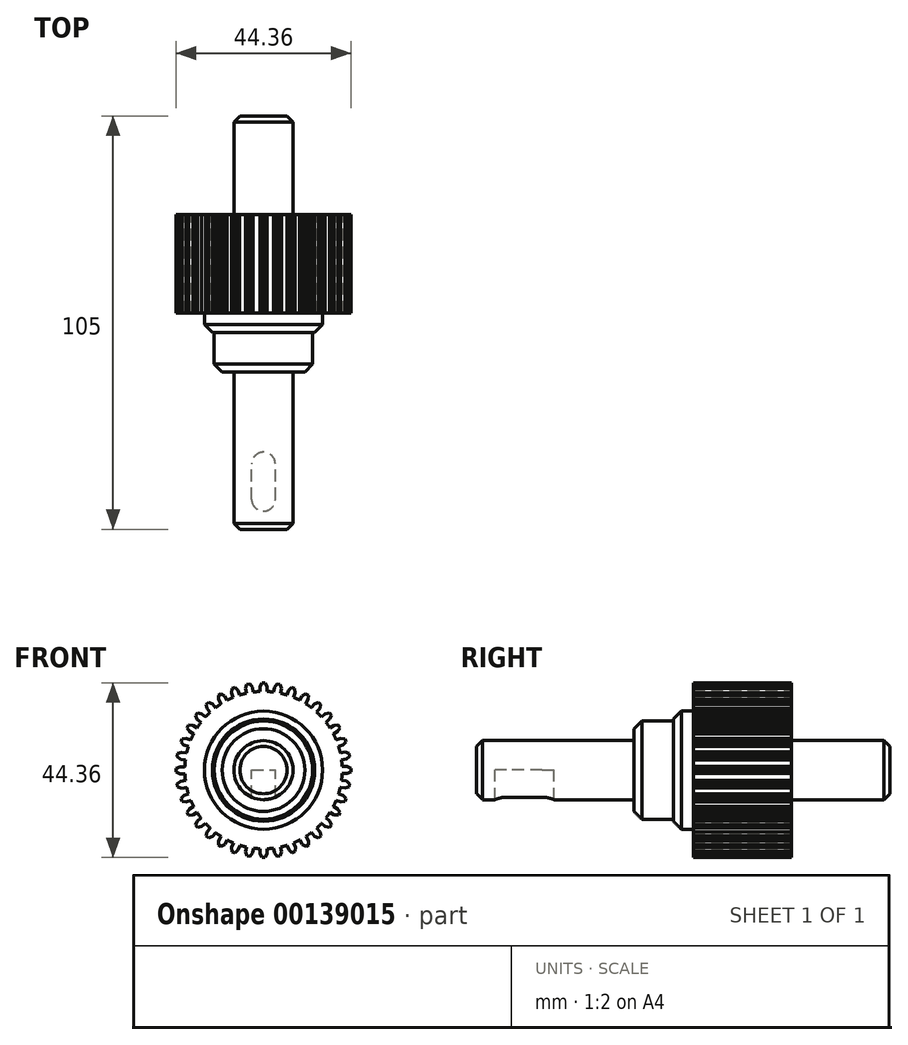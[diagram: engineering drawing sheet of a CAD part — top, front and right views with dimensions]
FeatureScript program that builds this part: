
annotation { "Feature Type Name" : "Feature", "Feature Type Description" : "" }
export const myFeature = defineFeature(function(context is Context, id is Id, definition is map)
    precondition{}
    {
        {
            var Q0;
            Q0=qCreatedBy(makeId("Front.planeOp"),FACE);
            var sketch = newSketch(context, id + "F0", { "sketchPlane" : qUnion([Q0])});
            skCircle(sketch, "E0", {"center": v(0, 0) * mm, "radius": 20 * mm});
            skLineSegment(sketch, "E1", {"start": v(-0.91, 19.98) * mm, "end": v(-0.91, 21.22) * mm});
            skLineSegment(sketch, "E2", {"start": v(-0.91, 21.22) * mm, "end": v(-0.42, 22.18) * mm});
            skLineSegment(sketch, "E3", {"start": v(-0.42, 22.18) * mm, "end": v(0.39, 22.18) * mm});
            skLineSegment(sketch, "E4", {"start": v(0.39, 22.18) * mm, "end": v(0.87, 21.22) * mm});
            skLineSegment(sketch, "E5", {"start": v(0.87, 21.22) * mm, "end": v(0.87, 19.98) * mm});
            skLineSegment(sketch, "E6", {"start": v(0, 0) * mm, "end": v(-0.02, 25.08) * mm});
            skPoint(sketch, "E6.endSnap0", {"position": v(-0.02, 22.18) * mm});
            skLineSegment(sketch, "E7.1.0", {"start": v(-4.37, 19.52) * mm, "end": v(-4.58, 20.74) * mm});
            skLineSegment(sketch, "E7.1.1", {"start": v(-4.58, 20.74) * mm, "end": v(-4.27, 21.77) * mm});
            skLineSegment(sketch, "E7.1.2", {"start": v(-4.27, 21.77) * mm, "end": v(-3.47, 21.91) * mm});
            skLineSegment(sketch, "E7.1.3", {"start": v(-3.47, 21.91) * mm, "end": v(-2.83, 21.05) * mm});
            skLineSegment(sketch, "E7.1.4", {"start": v(-2.83, 21.05) * mm, "end": v(-2.61, 19.83) * mm});
            skLineSegment(sketch, "E7.2.0", {"start": v(-7.69, 18.46) * mm, "end": v(-8.11, 19.63) * mm});
            skLineSegment(sketch, "E7.2.1", {"start": v(-8.11, 19.63) * mm, "end": v(-7.98, 20.7) * mm});
            skLineSegment(sketch, "E7.2.2", {"start": v(-7.98, 20.7) * mm, "end": v(-7.22, 20.98) * mm});
            skLineSegment(sketch, "E7.2.3", {"start": v(-7.22, 20.98) * mm, "end": v(-6.44, 20.24) * mm});
            skLineSegment(sketch, "E7.2.4", {"start": v(-6.44, 20.24) * mm, "end": v(-6.01, 19.07) * mm});
            skLineSegment(sketch, "E7.3.0", {"start": v(-10.78, 16.85) * mm, "end": v(-11.4, 17.92) * mm});
            skLineSegment(sketch, "E7.3.1", {"start": v(-11.4, 17.92) * mm, "end": v(-11.46, 19) * mm});
            skLineSegment(sketch, "E7.3.2", {"start": v(-11.46, 19) * mm, "end": v(-10.76, 19.4) * mm});
            skLineSegment(sketch, "E7.3.3", {"start": v(-10.76, 19.4) * mm, "end": v(-9.86, 18.81) * mm});
            skLineSegment(sketch, "E7.3.4", {"start": v(-9.86, 18.81) * mm, "end": v(-9.24, 17.74) * mm});
            skLineSegment(sketch, "E7.4.0", {"start": v(-13.54, 14.72) * mm, "end": v(-14.34, 15.67) * mm});
            skLineSegment(sketch, "E7.4.1", {"start": v(-14.34, 15.67) * mm, "end": v(-14.58, 16.72) * mm});
            skLineSegment(sketch, "E7.4.2", {"start": v(-14.58, 16.72) * mm, "end": v(-13.96, 17.24) * mm});
            skLineSegment(sketch, "E7.4.3", {"start": v(-13.96, 17.24) * mm, "end": v(-12.97, 16.82) * mm});
            skLineSegment(sketch, "E7.4.4", {"start": v(-12.97, 16.82) * mm, "end": v(-12.18, 15.87) * mm});
            skLineSegment(sketch, "E7.5.0", {"start": v(-15.9, 12.14) * mm, "end": v(-16.84, 12.94) * mm});
            skLineSegment(sketch, "E7.5.1", {"start": v(-16.84, 12.94) * mm, "end": v(-17.26, 13.93) * mm});
            skLineSegment(sketch, "E7.5.2", {"start": v(-17.26, 13.93) * mm, "end": v(-16.74, 14.55) * mm});
            skLineSegment(sketch, "E7.5.3", {"start": v(-16.74, 14.55) * mm, "end": v(-15.7, 14.3) * mm});
            skLineSegment(sketch, "E7.5.4", {"start": v(-15.7, 14.3) * mm, "end": v(-14.75, 13.51) * mm});
            skLineSegment(sketch, "E7.6.0", {"start": v(-17.76, 9.2) * mm, "end": v(-18.83, 9.82) * mm});
            skLineSegment(sketch, "E7.6.1", {"start": v(-18.83, 9.82) * mm, "end": v(-19.42, 10.72) * mm});
            skLineSegment(sketch, "E7.6.2", {"start": v(-19.42, 10.72) * mm, "end": v(-19.02, 11.43) * mm});
            skLineSegment(sketch, "E7.6.3", {"start": v(-19.02, 11.43) * mm, "end": v(-17.94, 11.37) * mm});
            skLineSegment(sketch, "E7.6.4", {"start": v(-17.94, 11.37) * mm, "end": v(-16.87, 10.75) * mm});
            skLineSegment(sketch, "E7.7.0", {"start": v(-19.09, 5.98) * mm, "end": v(-20.25, 6.4) * mm});
            skLineSegment(sketch, "E7.7.1", {"start": v(-20.25, 6.4) * mm, "end": v(-20.99, 7.19) * mm});
            skLineSegment(sketch, "E7.7.2", {"start": v(-20.99, 7.19) * mm, "end": v(-20.71, 7.95) * mm});
            skLineSegment(sketch, "E7.7.3", {"start": v(-20.71, 7.95) * mm, "end": v(-19.64, 8.08) * mm});
            skLineSegment(sketch, "E7.7.4", {"start": v(-19.64, 8.08) * mm, "end": v(-18.48, 7.65) * mm});
            skLineSegment(sketch, "E7.8.0", {"start": v(-19.83, 2.57) * mm, "end": v(-21.06, 2.79) * mm});
            skLineSegment(sketch, "E7.8.1", {"start": v(-21.06, 2.79) * mm, "end": v(-21.92, 3.44) * mm});
            skLineSegment(sketch, "E7.8.2", {"start": v(-21.92, 3.44) * mm, "end": v(-21.78, 4.23) * mm});
            skLineSegment(sketch, "E7.8.3", {"start": v(-21.78, 4.23) * mm, "end": v(-20.75, 4.54) * mm});
            skLineSegment(sketch, "E7.8.4", {"start": v(-20.75, 4.54) * mm, "end": v(-19.53, 4.33) * mm});
            skLineSegment(sketch, "E7.9.0", {"start": v(-19.98, -0.91) * mm, "end": v(-21.22, -0.91) * mm});
            skLineSegment(sketch, "E7.9.1", {"start": v(-21.22, -0.91) * mm, "end": v(-22.18, -0.42) * mm});
            skLineSegment(sketch, "E7.9.2", {"start": v(-22.18, -0.42) * mm, "end": v(-22.18, 0.39) * mm});
            skLineSegment(sketch, "E7.9.3", {"start": v(-22.18, 0.39) * mm, "end": v(-21.22, 0.87) * mm});
            skLineSegment(sketch, "E7.9.4", {"start": v(-21.22, 0.87) * mm, "end": v(-19.98, 0.87) * mm});
            skLineSegment(sketch, "E7.10.0", {"start": v(-19.52, -4.37) * mm, "end": v(-20.74, -4.58) * mm});
            skLineSegment(sketch, "E7.10.1", {"start": v(-20.74, -4.58) * mm, "end": v(-21.77, -4.27) * mm});
            skLineSegment(sketch, "E7.10.2", {"start": v(-21.77, -4.27) * mm, "end": v(-21.91, -3.47) * mm});
            skLineSegment(sketch, "E7.10.3", {"start": v(-21.91, -3.47) * mm, "end": v(-21.05, -2.83) * mm});
            skLineSegment(sketch, "E7.10.4", {"start": v(-21.05, -2.83) * mm, "end": v(-19.83, -2.61) * mm});
            skLineSegment(sketch, "E7.11.0", {"start": v(-18.46, -7.69) * mm, "end": v(-19.63, -8.11) * mm});
            skLineSegment(sketch, "E7.11.1", {"start": v(-19.63, -8.11) * mm, "end": v(-20.7, -7.98) * mm});
            skLineSegment(sketch, "E7.11.2", {"start": v(-20.7, -7.98) * mm, "end": v(-20.98, -7.22) * mm});
            skLineSegment(sketch, "E7.11.3", {"start": v(-20.98, -7.22) * mm, "end": v(-20.24, -6.44) * mm});
            skLineSegment(sketch, "E7.11.4", {"start": v(-20.24, -6.44) * mm, "end": v(-19.07, -6.01) * mm});
            skLineSegment(sketch, "E7.12.0", {"start": v(-16.85, -10.78) * mm, "end": v(-17.92, -11.4) * mm});
            skLineSegment(sketch, "E7.12.1", {"start": v(-17.92, -11.4) * mm, "end": v(-19, -11.46) * mm});
            skLineSegment(sketch, "E7.12.2", {"start": v(-19, -11.46) * mm, "end": v(-19.4, -10.76) * mm});
            skLineSegment(sketch, "E7.12.3", {"start": v(-19.4, -10.76) * mm, "end": v(-18.81, -9.86) * mm});
            skLineSegment(sketch, "E7.12.4", {"start": v(-18.81, -9.86) * mm, "end": v(-17.74, -9.24) * mm});
            skLineSegment(sketch, "E7.13.0", {"start": v(-14.72, -13.54) * mm, "end": v(-15.67, -14.34) * mm});
            skLineSegment(sketch, "E7.13.1", {"start": v(-15.67, -14.34) * mm, "end": v(-16.72, -14.58) * mm});
            skLineSegment(sketch, "E7.13.2", {"start": v(-16.72, -14.58) * mm, "end": v(-17.24, -13.96) * mm});
            skLineSegment(sketch, "E7.13.3", {"start": v(-17.24, -13.96) * mm, "end": v(-16.82, -12.97) * mm});
            skLineSegment(sketch, "E7.13.4", {"start": v(-16.82, -12.97) * mm, "end": v(-15.87, -12.18) * mm});
            skLineSegment(sketch, "E7.14.0", {"start": v(-12.14, -15.9) * mm, "end": v(-12.94, -16.84) * mm});
            skLineSegment(sketch, "E7.14.1", {"start": v(-12.94, -16.84) * mm, "end": v(-13.93, -17.26) * mm});
            skLineSegment(sketch, "E7.14.2", {"start": v(-13.93, -17.26) * mm, "end": v(-14.55, -16.74) * mm});
            skLineSegment(sketch, "E7.14.3", {"start": v(-14.55, -16.74) * mm, "end": v(-14.3, -15.7) * mm});
            skLineSegment(sketch, "E7.14.4", {"start": v(-14.3, -15.7) * mm, "end": v(-13.51, -14.75) * mm});
            skLineSegment(sketch, "E7.15.0", {"start": v(-9.2, -17.76) * mm, "end": v(-9.82, -18.83) * mm});
            skLineSegment(sketch, "E7.15.1", {"start": v(-9.82, -18.83) * mm, "end": v(-10.72, -19.42) * mm});
            skLineSegment(sketch, "E7.15.2", {"start": v(-10.72, -19.42) * mm, "end": v(-11.43, -19.02) * mm});
            skLineSegment(sketch, "E7.15.3", {"start": v(-11.43, -19.02) * mm, "end": v(-11.37, -17.94) * mm});
            skLineSegment(sketch, "E7.15.4", {"start": v(-11.37, -17.94) * mm, "end": v(-10.75, -16.87) * mm});
            skLineSegment(sketch, "E7.16.0", {"start": v(-5.98, -19.09) * mm, "end": v(-6.4, -20.25) * mm});
            skLineSegment(sketch, "E7.16.1", {"start": v(-6.4, -20.25) * mm, "end": v(-7.19, -20.99) * mm});
            skLineSegment(sketch, "E7.16.2", {"start": v(-7.19, -20.99) * mm, "end": v(-7.95, -20.71) * mm});
            skLineSegment(sketch, "E7.16.3", {"start": v(-7.95, -20.71) * mm, "end": v(-8.08, -19.64) * mm});
            skLineSegment(sketch, "E7.16.4", {"start": v(-8.08, -19.64) * mm, "end": v(-7.65, -18.48) * mm});
            skLineSegment(sketch, "E7.17.0", {"start": v(-2.57, -19.83) * mm, "end": v(-2.79, -21.06) * mm});
            skLineSegment(sketch, "E7.17.1", {"start": v(-2.79, -21.06) * mm, "end": v(-3.44, -21.92) * mm});
            skLineSegment(sketch, "E7.17.2", {"start": v(-3.44, -21.92) * mm, "end": v(-4.23, -21.78) * mm});
            skLineSegment(sketch, "E7.17.3", {"start": v(-4.23, -21.78) * mm, "end": v(-4.54, -20.75) * mm});
            skLineSegment(sketch, "E7.17.4", {"start": v(-4.54, -20.75) * mm, "end": v(-4.33, -19.53) * mm});
            skLineSegment(sketch, "E7.18.0", {"start": v(0.91, -19.98) * mm, "end": v(0.91, -21.22) * mm});
            skLineSegment(sketch, "E7.18.1", {"start": v(0.91, -21.22) * mm, "end": v(0.42, -22.18) * mm});
            skLineSegment(sketch, "E7.18.2", {"start": v(0.42, -22.18) * mm, "end": v(-0.39, -22.18) * mm});
            skLineSegment(sketch, "E7.18.3", {"start": v(-0.39, -22.18) * mm, "end": v(-0.87, -21.22) * mm});
            skLineSegment(sketch, "E7.18.4", {"start": v(-0.87, -21.22) * mm, "end": v(-0.87, -19.98) * mm});
            skLineSegment(sketch, "E7.19.0", {"start": v(4.37, -19.52) * mm, "end": v(4.58, -20.74) * mm});
            skLineSegment(sketch, "E7.19.1", {"start": v(4.58, -20.74) * mm, "end": v(4.27, -21.77) * mm});
            skLineSegment(sketch, "E7.19.2", {"start": v(4.27, -21.77) * mm, "end": v(3.47, -21.91) * mm});
            skLineSegment(sketch, "E7.19.3", {"start": v(3.47, -21.91) * mm, "end": v(2.83, -21.05) * mm});
            skLineSegment(sketch, "E7.19.4", {"start": v(2.83, -21.05) * mm, "end": v(2.61, -19.83) * mm});
            skLineSegment(sketch, "E7.20.0", {"start": v(7.69, -18.46) * mm, "end": v(8.11, -19.63) * mm});
            skLineSegment(sketch, "E7.20.1", {"start": v(8.11, -19.63) * mm, "end": v(7.98, -20.7) * mm});
            skLineSegment(sketch, "E7.20.2", {"start": v(7.98, -20.7) * mm, "end": v(7.22, -20.98) * mm});
            skLineSegment(sketch, "E7.20.3", {"start": v(7.22, -20.98) * mm, "end": v(6.44, -20.24) * mm});
            skLineSegment(sketch, "E7.20.4", {"start": v(6.44, -20.24) * mm, "end": v(6.01, -19.07) * mm});
            skLineSegment(sketch, "E7.21.0", {"start": v(10.78, -16.85) * mm, "end": v(11.4, -17.92) * mm});
            skLineSegment(sketch, "E7.21.1", {"start": v(11.4, -17.92) * mm, "end": v(11.46, -19) * mm});
            skLineSegment(sketch, "E7.21.2", {"start": v(11.46, -19) * mm, "end": v(10.76, -19.4) * mm});
            skLineSegment(sketch, "E7.21.3", {"start": v(10.76, -19.4) * mm, "end": v(9.86, -18.81) * mm});
            skLineSegment(sketch, "E7.21.4", {"start": v(9.86, -18.81) * mm, "end": v(9.24, -17.74) * mm});
            skLineSegment(sketch, "E7.22.0", {"start": v(13.54, -14.72) * mm, "end": v(14.34, -15.67) * mm});
            skLineSegment(sketch, "E7.22.1", {"start": v(14.34, -15.67) * mm, "end": v(14.58, -16.72) * mm});
            skLineSegment(sketch, "E7.22.2", {"start": v(14.58, -16.72) * mm, "end": v(13.96, -17.24) * mm});
            skLineSegment(sketch, "E7.22.3", {"start": v(13.96, -17.24) * mm, "end": v(12.97, -16.82) * mm});
            skLineSegment(sketch, "E7.22.4", {"start": v(12.97, -16.82) * mm, "end": v(12.18, -15.87) * mm});
            skLineSegment(sketch, "E7.23.0", {"start": v(15.9, -12.14) * mm, "end": v(16.84, -12.94) * mm});
            skLineSegment(sketch, "E7.23.1", {"start": v(16.84, -12.94) * mm, "end": v(17.26, -13.93) * mm});
            skLineSegment(sketch, "E7.23.2", {"start": v(17.26, -13.93) * mm, "end": v(16.74, -14.55) * mm});
            skLineSegment(sketch, "E7.23.3", {"start": v(16.74, -14.55) * mm, "end": v(15.7, -14.3) * mm});
            skLineSegment(sketch, "E7.23.4", {"start": v(15.7, -14.3) * mm, "end": v(14.75, -13.51) * mm});
            skLineSegment(sketch, "E7.24.0", {"start": v(17.76, -9.2) * mm, "end": v(18.83, -9.82) * mm});
            skLineSegment(sketch, "E7.24.1", {"start": v(18.83, -9.82) * mm, "end": v(19.42, -10.72) * mm});
            skLineSegment(sketch, "E7.24.2", {"start": v(19.42, -10.72) * mm, "end": v(19.02, -11.43) * mm});
            skLineSegment(sketch, "E7.24.3", {"start": v(19.02, -11.43) * mm, "end": v(17.94, -11.37) * mm});
            skLineSegment(sketch, "E7.24.4", {"start": v(17.94, -11.37) * mm, "end": v(16.87, -10.75) * mm});
            skLineSegment(sketch, "E7.25.0", {"start": v(19.09, -5.98) * mm, "end": v(20.25, -6.4) * mm});
            skLineSegment(sketch, "E7.25.1", {"start": v(20.25, -6.4) * mm, "end": v(20.99, -7.19) * mm});
            skLineSegment(sketch, "E7.25.2", {"start": v(20.99, -7.19) * mm, "end": v(20.71, -7.95) * mm});
            skLineSegment(sketch, "E7.25.3", {"start": v(20.71, -7.95) * mm, "end": v(19.64, -8.08) * mm});
            skLineSegment(sketch, "E7.25.4", {"start": v(19.64, -8.08) * mm, "end": v(18.48, -7.65) * mm});
            skLineSegment(sketch, "E7.26.0", {"start": v(19.83, -2.57) * mm, "end": v(21.06, -2.79) * mm});
            skLineSegment(sketch, "E7.26.1", {"start": v(21.06, -2.79) * mm, "end": v(21.92, -3.44) * mm});
            skLineSegment(sketch, "E7.26.2", {"start": v(21.92, -3.44) * mm, "end": v(21.78, -4.23) * mm});
            skLineSegment(sketch, "E7.26.3", {"start": v(21.78, -4.23) * mm, "end": v(20.75, -4.54) * mm});
            skLineSegment(sketch, "E7.26.4", {"start": v(20.75, -4.54) * mm, "end": v(19.53, -4.33) * mm});
            skLineSegment(sketch, "E7.27.0", {"start": v(19.98, 0.91) * mm, "end": v(21.22, 0.91) * mm});
            skLineSegment(sketch, "E7.27.1", {"start": v(21.22, 0.91) * mm, "end": v(22.18, 0.42) * mm});
            skLineSegment(sketch, "E7.27.2", {"start": v(22.18, 0.42) * mm, "end": v(22.18, -0.39) * mm});
            skLineSegment(sketch, "E7.27.3", {"start": v(22.18, -0.39) * mm, "end": v(21.22, -0.87) * mm});
            skLineSegment(sketch, "E7.27.4", {"start": v(21.22, -0.87) * mm, "end": v(19.98, -0.87) * mm});
            skLineSegment(sketch, "E7.28.0", {"start": v(19.52, 4.37) * mm, "end": v(20.74, 4.58) * mm});
            skLineSegment(sketch, "E7.28.1", {"start": v(20.74, 4.58) * mm, "end": v(21.77, 4.27) * mm});
            skLineSegment(sketch, "E7.28.2", {"start": v(21.77, 4.27) * mm, "end": v(21.91, 3.47) * mm});
            skLineSegment(sketch, "E7.28.3", {"start": v(21.91, 3.47) * mm, "end": v(21.05, 2.83) * mm});
            skLineSegment(sketch, "E7.28.4", {"start": v(21.05, 2.83) * mm, "end": v(19.83, 2.61) * mm});
            skLineSegment(sketch, "E7.29.0", {"start": v(18.46, 7.69) * mm, "end": v(19.63, 8.11) * mm});
            skLineSegment(sketch, "E7.29.1", {"start": v(19.63, 8.11) * mm, "end": v(20.7, 7.98) * mm});
            skLineSegment(sketch, "E7.29.2", {"start": v(20.7, 7.98) * mm, "end": v(20.98, 7.22) * mm});
            skLineSegment(sketch, "E7.29.3", {"start": v(20.98, 7.22) * mm, "end": v(20.24, 6.44) * mm});
            skLineSegment(sketch, "E7.29.4", {"start": v(20.24, 6.44) * mm, "end": v(19.07, 6.01) * mm});
            skLineSegment(sketch, "E7.30.0", {"start": v(16.85, 10.78) * mm, "end": v(17.92, 11.4) * mm});
            skLineSegment(sketch, "E7.30.1", {"start": v(17.92, 11.4) * mm, "end": v(19, 11.46) * mm});
            skLineSegment(sketch, "E7.30.2", {"start": v(19, 11.46) * mm, "end": v(19.4, 10.76) * mm});
            skLineSegment(sketch, "E7.30.3", {"start": v(19.4, 10.76) * mm, "end": v(18.81, 9.86) * mm});
            skLineSegment(sketch, "E7.30.4", {"start": v(18.81, 9.86) * mm, "end": v(17.74, 9.24) * mm});
            skLineSegment(sketch, "E7.31.0", {"start": v(14.72, 13.54) * mm, "end": v(15.67, 14.34) * mm});
            skLineSegment(sketch, "E7.31.1", {"start": v(15.67, 14.34) * mm, "end": v(16.72, 14.58) * mm});
            skLineSegment(sketch, "E7.31.2", {"start": v(16.72, 14.58) * mm, "end": v(17.24, 13.96) * mm});
            skLineSegment(sketch, "E7.31.3", {"start": v(17.24, 13.96) * mm, "end": v(16.82, 12.97) * mm});
            skLineSegment(sketch, "E7.31.4", {"start": v(16.82, 12.97) * mm, "end": v(15.87, 12.18) * mm});
            skLineSegment(sketch, "E7.32.0", {"start": v(12.14, 15.9) * mm, "end": v(12.94, 16.84) * mm});
            skLineSegment(sketch, "E7.32.1", {"start": v(12.94, 16.84) * mm, "end": v(13.93, 17.26) * mm});
            skLineSegment(sketch, "E7.32.2", {"start": v(13.93, 17.26) * mm, "end": v(14.55, 16.74) * mm});
            skLineSegment(sketch, "E7.32.3", {"start": v(14.55, 16.74) * mm, "end": v(14.3, 15.7) * mm});
            skLineSegment(sketch, "E7.32.4", {"start": v(14.3, 15.7) * mm, "end": v(13.51, 14.75) * mm});
            skLineSegment(sketch, "E7.33.0", {"start": v(9.2, 17.76) * mm, "end": v(9.82, 18.83) * mm});
            skLineSegment(sketch, "E7.33.1", {"start": v(9.82, 18.83) * mm, "end": v(10.72, 19.42) * mm});
            skLineSegment(sketch, "E7.33.2", {"start": v(10.72, 19.42) * mm, "end": v(11.43, 19.02) * mm});
            skLineSegment(sketch, "E7.33.3", {"start": v(11.43, 19.02) * mm, "end": v(11.37, 17.94) * mm});
            skLineSegment(sketch, "E7.33.4", {"start": v(11.37, 17.94) * mm, "end": v(10.75, 16.87) * mm});
            skLineSegment(sketch, "E7.34.0", {"start": v(5.98, 19.09) * mm, "end": v(6.4, 20.25) * mm});
            skLineSegment(sketch, "E7.34.1", {"start": v(6.4, 20.25) * mm, "end": v(7.19, 20.99) * mm});
            skLineSegment(sketch, "E7.34.2", {"start": v(7.19, 20.99) * mm, "end": v(7.95, 20.71) * mm});
            skLineSegment(sketch, "E7.34.3", {"start": v(7.95, 20.71) * mm, "end": v(8.08, 19.64) * mm});
            skLineSegment(sketch, "E7.34.4", {"start": v(8.08, 19.64) * mm, "end": v(7.65, 18.48) * mm});
            skLineSegment(sketch, "E7.35.0", {"start": v(2.57, 19.83) * mm, "end": v(2.79, 21.06) * mm});
            skLineSegment(sketch, "E7.35.1", {"start": v(2.79, 21.06) * mm, "end": v(3.44, 21.92) * mm});
            skLineSegment(sketch, "E7.35.2", {"start": v(3.44, 21.92) * mm, "end": v(4.23, 21.78) * mm});
            skLineSegment(sketch, "E7.35.3", {"start": v(4.23, 21.78) * mm, "end": v(4.54, 20.75) * mm});
            skLineSegment(sketch, "E7.35.4", {"start": v(4.54, 20.75) * mm, "end": v(4.33, 19.53) * mm});
            skSolve(sketch);
        }
        {
            var Q0;
            Q0 = qSketchRegion(id + "F0", true);
            extrude(context, id + "F1", {"entities" : qUnion([Q0]), "depth" : 25 * mm});
        }
        {
            var Q0;
            Q0=makeQuery(id+"F1.opExtrude","CAP_FACE",FACE,{"disambiguationData":[OSD([sQuery(id+"F0.wireOp",EDGE,"E0"),sQuery(id+"F0.wireOp",EDGE,"E1"),sQuery(id+"F0.wireOp",EDGE,"E2"),sQuery(id+"F0.wireOp",EDGE,"E3"),sQuery(id+"F0.wireOp",EDGE,"E4"),sQuery(id+"F0.wireOp",EDGE,"E5"),sQuery(id+"F0.wireOp",EDGE,"E7.1.0"),sQuery(id+"F0.wireOp",EDGE,"E7.1.1"),sQuery(id+"F0.wireOp",EDGE,"E7.1.2"),sQuery(id+"F0.wireOp",EDGE,"E7.1.3"),sQuery(id+"F0.wireOp",EDGE,"E7.1.4"),sQuery(id+"F0.wireOp",EDGE,"E7.2.0"),sQuery(id+"F0.wireOp",EDGE,"E7.2.1"),sQuery(id+"F0.wireOp",EDGE,"E7.2.2"),sQuery(id+"F0.wireOp",EDGE,"E7.2.3"),sQuery(id+"F0.wireOp",EDGE,"E7.2.4"),sQuery(id+"F0.wireOp",EDGE,"E7.3.0"),sQuery(id+"F0.wireOp",EDGE,"E7.3.1"),sQuery(id+"F0.wireOp",EDGE,"E7.3.2"),sQuery(id+"F0.wireOp",EDGE,"E7.3.3"),sQuery(id+"F0.wireOp",EDGE,"E7.3.4"),sQuery(id+"F0.wireOp",EDGE,"E7.4.0"),sQuery(id+"F0.wireOp",EDGE,"E7.4.1"),sQuery(id+"F0.wireOp",EDGE,"E7.4.2"),sQuery(id+"F0.wireOp",EDGE,"E7.4.3"),sQuery(id+"F0.wireOp",EDGE,"E7.4.4"),sQuery(id+"F0.wireOp",EDGE,"E7.5.0"),sQuery(id+"F0.wireOp",EDGE,"E7.5.1"),sQuery(id+"F0.wireOp",EDGE,"E7.5.2"),sQuery(id+"F0.wireOp",EDGE,"E7.5.3"),sQuery(id+"F0.wireOp",EDGE,"E7.5.4"),sQuery(id+"F0.wireOp",EDGE,"E7.6.0"),sQuery(id+"F0.wireOp",EDGE,"E7.6.1"),sQuery(id+"F0.wireOp",EDGE,"E7.6.2"),sQuery(id+"F0.wireOp",EDGE,"E7.6.3"),sQuery(id+"F0.wireOp",EDGE,"E7.6.4"),sQuery(id+"F0.wireOp",EDGE,"E7.7.0"),sQuery(id+"F0.wireOp",EDGE,"E7.7.1"),sQuery(id+"F0.wireOp",EDGE,"E7.7.2"),sQuery(id+"F0.wireOp",EDGE,"E7.7.3"),sQuery(id+"F0.wireOp",EDGE,"E7.7.4"),sQuery(id+"F0.wireOp",EDGE,"E7.8.0"),sQuery(id+"F0.wireOp",EDGE,"E7.8.1"),sQuery(id+"F0.wireOp",EDGE,"E7.8.2"),sQuery(id+"F0.wireOp",EDGE,"E7.8.3"),sQuery(id+"F0.wireOp",EDGE,"E7.8.4"),sQuery(id+"F0.wireOp",EDGE,"E7.9.0"),sQuery(id+"F0.wireOp",EDGE,"E7.9.1"),sQuery(id+"F0.wireOp",EDGE,"E7.9.2"),sQuery(id+"F0.wireOp",EDGE,"E7.9.3"),sQuery(id+"F0.wireOp",EDGE,"E7.9.4"),sQuery(id+"F0.wireOp",EDGE,"E7.10.0"),sQuery(id+"F0.wireOp",EDGE,"E7.10.1"),sQuery(id+"F0.wireOp",EDGE,"E7.10.2"),sQuery(id+"F0.wireOp",EDGE,"E7.10.3"),sQuery(id+"F0.wireOp",EDGE,"E7.10.4"),sQuery(id+"F0.wireOp",EDGE,"E7.11.0"),sQuery(id+"F0.wireOp",EDGE,"E7.11.1"),sQuery(id+"F0.wireOp",EDGE,"E7.11.2"),sQuery(id+"F0.wireOp",EDGE,"E7.11.3"),sQuery(id+"F0.wireOp",EDGE,"E7.11.4"),sQuery(id+"F0.wireOp",EDGE,"E7.12.0"),sQuery(id+"F0.wireOp",EDGE,"E7.12.1"),sQuery(id+"F0.wireOp",EDGE,"E7.12.2"),sQuery(id+"F0.wireOp",EDGE,"E7.12.3"),sQuery(id+"F0.wireOp",EDGE,"E7.12.4"),sQuery(id+"F0.wireOp",EDGE,"E7.13.0"),sQuery(id+"F0.wireOp",EDGE,"E7.13.1"),sQuery(id+"F0.wireOp",EDGE,"E7.13.2"),sQuery(id+"F0.wireOp",EDGE,"E7.13.3"),sQuery(id+"F0.wireOp",EDGE,"E7.13.4"),sQuery(id+"F0.wireOp",EDGE,"E7.14.0"),sQuery(id+"F0.wireOp",EDGE,"E7.14.1"),sQuery(id+"F0.wireOp",EDGE,"E7.14.2"),sQuery(id+"F0.wireOp",EDGE,"E7.14.3"),sQuery(id+"F0.wireOp",EDGE,"E7.14.4"),sQuery(id+"F0.wireOp",EDGE,"E7.15.0"),sQuery(id+"F0.wireOp",EDGE,"E7.15.1"),sQuery(id+"F0.wireOp",EDGE,"E7.15.2"),sQuery(id+"F0.wireOp",EDGE,"E7.15.3"),sQuery(id+"F0.wireOp",EDGE,"E7.15.4"),sQuery(id+"F0.wireOp",EDGE,"E7.16.0"),sQuery(id+"F0.wireOp",EDGE,"E7.16.1"),sQuery(id+"F0.wireOp",EDGE,"E7.16.2"),sQuery(id+"F0.wireOp",EDGE,"E7.16.3"),sQuery(id+"F0.wireOp",EDGE,"E7.16.4"),sQuery(id+"F0.wireOp",EDGE,"E7.17.0"),sQuery(id+"F0.wireOp",EDGE,"E7.17.1"),sQuery(id+"F0.wireOp",EDGE,"E7.17.2"),sQuery(id+"F0.wireOp",EDGE,"E7.17.3"),sQuery(id+"F0.wireOp",EDGE,"E7.17.4"),sQuery(id+"F0.wireOp",EDGE,"E7.18.0"),sQuery(id+"F0.wireOp",EDGE,"E7.18.1"),sQuery(id+"F0.wireOp",EDGE,"E7.18.2"),sQuery(id+"F0.wireOp",EDGE,"E7.18.3"),sQuery(id+"F0.wireOp",EDGE,"E7.18.4"),sQuery(id+"F0.wireOp",EDGE,"E7.19.0"),sQuery(id+"F0.wireOp",EDGE,"E7.19.1"),sQuery(id+"F0.wireOp",EDGE,"E7.19.2"),sQuery(id+"F0.wireOp",EDGE,"E7.19.3"),sQuery(id+"F0.wireOp",EDGE,"E7.19.4"),sQuery(id+"F0.wireOp",EDGE,"E7.20.0"),sQuery(id+"F0.wireOp",EDGE,"E7.20.1"),sQuery(id+"F0.wireOp",EDGE,"E7.20.2"),sQuery(id+"F0.wireOp",EDGE,"E7.20.3"),sQuery(id+"F0.wireOp",EDGE,"E7.20.4"),sQuery(id+"F0.wireOp",EDGE,"E7.21.0"),sQuery(id+"F0.wireOp",EDGE,"E7.21.1"),sQuery(id+"F0.wireOp",EDGE,"E7.21.2"),sQuery(id+"F0.wireOp",EDGE,"E7.21.3"),sQuery(id+"F0.wireOp",EDGE,"E7.21.4"),sQuery(id+"F0.wireOp",EDGE,"E7.22.0"),sQuery(id+"F0.wireOp",EDGE,"E7.22.1"),sQuery(id+"F0.wireOp",EDGE,"E7.22.2"),sQuery(id+"F0.wireOp",EDGE,"E7.22.3"),sQuery(id+"F0.wireOp",EDGE,"E7.22.4"),sQuery(id+"F0.wireOp",EDGE,"E7.23.0"),sQuery(id+"F0.wireOp",EDGE,"E7.23.1"),sQuery(id+"F0.wireOp",EDGE,"E7.23.2"),sQuery(id+"F0.wireOp",EDGE,"E7.23.3"),sQuery(id+"F0.wireOp",EDGE,"E7.23.4"),sQuery(id+"F0.wireOp",EDGE,"E7.24.0"),sQuery(id+"F0.wireOp",EDGE,"E7.24.1"),sQuery(id+"F0.wireOp",EDGE,"E7.24.2"),sQuery(id+"F0.wireOp",EDGE,"E7.24.3"),sQuery(id+"F0.wireOp",EDGE,"E7.24.4"),sQuery(id+"F0.wireOp",EDGE,"E7.25.0"),sQuery(id+"F0.wireOp",EDGE,"E7.25.1"),sQuery(id+"F0.wireOp",EDGE,"E7.25.2"),sQuery(id+"F0.wireOp",EDGE,"E7.25.3"),sQuery(id+"F0.wireOp",EDGE,"E7.25.4"),sQuery(id+"F0.wireOp",EDGE,"E7.26.0"),sQuery(id+"F0.wireOp",EDGE,"E7.26.1"),sQuery(id+"F0.wireOp",EDGE,"E7.26.2"),sQuery(id+"F0.wireOp",EDGE,"E7.26.3"),sQuery(id+"F0.wireOp",EDGE,"E7.26.4"),sQuery(id+"F0.wireOp",EDGE,"E7.27.0"),sQuery(id+"F0.wireOp",EDGE,"E7.27.1"),sQuery(id+"F0.wireOp",EDGE,"E7.27.2"),sQuery(id+"F0.wireOp",EDGE,"E7.27.3"),sQuery(id+"F0.wireOp",EDGE,"E7.27.4"),sQuery(id+"F0.wireOp",EDGE,"E7.28.0"),sQuery(id+"F0.wireOp",EDGE,"E7.28.1"),sQuery(id+"F0.wireOp",EDGE,"E7.28.2"),sQuery(id+"F0.wireOp",EDGE,"E7.28.3"),sQuery(id+"F0.wireOp",EDGE,"E7.28.4"),sQuery(id+"F0.wireOp",EDGE,"E7.29.0"),sQuery(id+"F0.wireOp",EDGE,"E7.29.1"),sQuery(id+"F0.wireOp",EDGE,"E7.29.2"),sQuery(id+"F0.wireOp",EDGE,"E7.29.3"),sQuery(id+"F0.wireOp",EDGE,"E7.29.4"),sQuery(id+"F0.wireOp",EDGE,"E7.30.0"),sQuery(id+"F0.wireOp",EDGE,"E7.30.1"),sQuery(id+"F0.wireOp",EDGE,"E7.30.2"),sQuery(id+"F0.wireOp",EDGE,"E7.30.3"),sQuery(id+"F0.wireOp",EDGE,"E7.30.4"),sQuery(id+"F0.wireOp",EDGE,"E7.31.0"),sQuery(id+"F0.wireOp",EDGE,"E7.31.1"),sQuery(id+"F0.wireOp",EDGE,"E7.31.2"),sQuery(id+"F0.wireOp",EDGE,"E7.31.3"),sQuery(id+"F0.wireOp",EDGE,"E7.31.4"),sQuery(id+"F0.wireOp",EDGE,"E7.32.0"),sQuery(id+"F0.wireOp",EDGE,"E7.32.1"),sQuery(id+"F0.wireOp",EDGE,"E7.32.2"),sQuery(id+"F0.wireOp",EDGE,"E7.32.3"),sQuery(id+"F0.wireOp",EDGE,"E7.32.4"),sQuery(id+"F0.wireOp",EDGE,"E7.33.0"),sQuery(id+"F0.wireOp",EDGE,"E7.33.1"),sQuery(id+"F0.wireOp",EDGE,"E7.33.2"),sQuery(id+"F0.wireOp",EDGE,"E7.33.3"),sQuery(id+"F0.wireOp",EDGE,"E7.33.4"),sQuery(id+"F0.wireOp",EDGE,"E7.34.0"),sQuery(id+"F0.wireOp",EDGE,"E7.34.1"),sQuery(id+"F0.wireOp",EDGE,"E7.34.2"),sQuery(id+"F0.wireOp",EDGE,"E7.34.3"),sQuery(id+"F0.wireOp",EDGE,"E7.34.4"),sQuery(id+"F0.wireOp",EDGE,"E7.35.0"),sQuery(id+"F0.wireOp",EDGE,"E7.35.1"),sQuery(id+"F0.wireOp",EDGE,"E7.35.2"),sQuery(id+"F0.wireOp",EDGE,"E7.35.3"),sQuery(id+"F0.wireOp",EDGE,"E7.35.4")])],"isStart":false});
            var sketch = newSketch(context, id + "F2", { "sketchPlane" : qUnion([Q0])});
            skCircle(sketch, "E8", {"center": v(0, 0) * mm, "radius": 15 * mm});
            skSolve(sketch);
        }
        {
            var Q0;
            Q0 = qSketchRegion(id + "F2", true);
            extrude(context, id + "F3", {"entities" : qUnion([Q0]), "operationType" : NewBodyOperationType.ADD, "depth" : 5 * mm});
        }
        {
            var Q0;
            Q0=makeQuery(id+"F3.opExtrude","CAP_FACE",FACE,{"disambiguationData":[OSD([sQuery(id+"F2.wireOp",EDGE,"E8")])],"isStart":false});
            var sketch = newSketch(context, id + "F4", { "sketchPlane" : qUnion([Q0])});
            skCircle(sketch, "E9", {"center": v(0, 0) * mm, "radius": 12.5 * mm});
            skSolve(sketch);
        }
        {
            var Q0;
            Q0 = qSketchRegion(id + "F4", true);
            extrude(context, id + "F5", {"entities" : qUnion([Q0]), "operationType" : NewBodyOperationType.ADD, "depth" : 10 * mm});
        }
        {
            var Q0;
            Q0=makeQuery(id+"F5.opExtrude","CAP_FACE",FACE,{"disambiguationData":[OSD([sQuery(id+"F4.wireOp",EDGE,"E9")])],"isStart":false});
            var sketch = newSketch(context, id + "F6", { "sketchPlane" : qUnion([Q0])});
            skCircle(sketch, "E10", {"center": v(0, 0) * mm, "radius": 7.5 * mm});
            skSolve(sketch);
        }
        {
            var Q0;
            Q0 = qSketchRegion(id + "F6", true);
            extrude(context, id + "F7", {"entities" : qUnion([Q0]), "operationType" : NewBodyOperationType.ADD, "depth" : 40 * mm});
        }
        {
            var Q0;
            Q0=qCreatedBy(makeId("Top.planeOp"),FACE);
            var sketch = newSketch(context, id + "F8", { "sketchPlane" : qUnion([Q0])});
            skLineSegment(sketch, "E11.bottom", {"start": v(0, -60.39) * mm, "end": v(0, -60.39) * mm});
            skLineSegment(sketch, "E11.top", {"start": v(0, -75.39) * mm, "end": v(0, -75.39) * mm});
            skLineSegment(sketch, "E11.left", {"start": v(3, -63.39) * mm, "end": v(3, -72.39) * mm});
            skLineSegment(sketch, "E11.right", {"start": v(-3, -63.39) * mm, "end": v(-3, -72.39) * mm});
            skPoint(sketch, "E11.middle", {"position": v(0, -67.89) * mm});
            skPoint(sketch, "E12.visualSharp", {"position": v(-3, -75.39) * mm});
            skArc(sketch, "E12.filletArc", {"start": v(-3, -72.39) * mm, "mid": v(-2.12, -74.5) * mm, "end": v(0, -75.39) * mm});
            skPoint(sketch, "E13.visualSharp", {"position": v(3, -75.39) * mm});
            skArc(sketch, "E13.filletArc", {"start": v(0, -75.39) * mm, "mid": v(2.12, -74.5) * mm, "end": v(3, -72.39) * mm});
            skPoint(sketch, "E14.visualSharp", {"position": v(3, -60.39) * mm});
            skArc(sketch, "E14.filletArc", {"start": v(3, -63.39) * mm, "mid": v(2.12, -61.27) * mm, "end": v(0, -60.39) * mm});
            skPoint(sketch, "E15.visualSharp", {"position": v(-3, -60.39) * mm});
            skArc(sketch, "E15.filletArc", {"start": v(0, -60.39) * mm, "mid": v(-2.12, -61.27) * mm, "end": v(-3, -63.39) * mm});
            skSolve(sketch);
        }
        {
            var Q0;
            Q0 = qSketchRegion(id + "F8", true);
            extrude(context, id + "F9", {"entities" : qUnion([Q0]), "operationType" : NewBodyOperationType.REMOVE, "oppositeDirection" : true, "depth" : 25 * mm});
        }
        {
            var Q0;
            Q0=makeQuery(id+"F3.opExtrude","CAP_EDGE",EDGE,{"disambiguationData":[OSD([sQuery(id+"F2.wireOp",EDGE,"E8")])],"isStart":false});
            var Q1;
            Q1=makeQuery(id+"F5.opExtrude","CAP_EDGE",EDGE,{"disambiguationData":[OSD([sQuery(id+"F4.wireOp",EDGE,"E9")])],"isStart":false});
            chamfer(context, id + "F10", {"entities" : qUnion([Q0, Q1]), "width" : 2 * mm, "tangentPropagation" : true});
        }
        {
            var Q0;
            Q0=makeQuery(id+"F7.opExtrude","CAP_EDGE",EDGE,{"disambiguationData":[OSD([sQuery(id+"F6.wireOp",EDGE,"E10")])],"isStart":false});
            chamfer(context, id + "F11", {"entities" : qUnion([Q0]), "width" : 1.5 * mm, "tangentPropagation" : true});
        }
        {
            var Q0;
            Q0=makeQuery(id+"F1.opExtrude","CAP_FACE",FACE,{"disambiguationData":[OSD([sQuery(id+"F0.wireOp",EDGE,"E0"),sQuery(id+"F0.wireOp",EDGE,"E1"),sQuery(id+"F0.wireOp",EDGE,"E2"),sQuery(id+"F0.wireOp",EDGE,"E3"),sQuery(id+"F0.wireOp",EDGE,"E4"),sQuery(id+"F0.wireOp",EDGE,"E5"),sQuery(id+"F0.wireOp",EDGE,"E7.1.0"),sQuery(id+"F0.wireOp",EDGE,"E7.1.1"),sQuery(id+"F0.wireOp",EDGE,"E7.1.2"),sQuery(id+"F0.wireOp",EDGE,"E7.1.3"),sQuery(id+"F0.wireOp",EDGE,"E7.1.4"),sQuery(id+"F0.wireOp",EDGE,"E7.2.0"),sQuery(id+"F0.wireOp",EDGE,"E7.2.1"),sQuery(id+"F0.wireOp",EDGE,"E7.2.2"),sQuery(id+"F0.wireOp",EDGE,"E7.2.3"),sQuery(id+"F0.wireOp",EDGE,"E7.2.4"),sQuery(id+"F0.wireOp",EDGE,"E7.3.0"),sQuery(id+"F0.wireOp",EDGE,"E7.3.1"),sQuery(id+"F0.wireOp",EDGE,"E7.3.2"),sQuery(id+"F0.wireOp",EDGE,"E7.3.3"),sQuery(id+"F0.wireOp",EDGE,"E7.3.4"),sQuery(id+"F0.wireOp",EDGE,"E7.4.0"),sQuery(id+"F0.wireOp",EDGE,"E7.4.1"),sQuery(id+"F0.wireOp",EDGE,"E7.4.2"),sQuery(id+"F0.wireOp",EDGE,"E7.4.3"),sQuery(id+"F0.wireOp",EDGE,"E7.4.4"),sQuery(id+"F0.wireOp",EDGE,"E7.5.0"),sQuery(id+"F0.wireOp",EDGE,"E7.5.1"),sQuery(id+"F0.wireOp",EDGE,"E7.5.2"),sQuery(id+"F0.wireOp",EDGE,"E7.5.3"),sQuery(id+"F0.wireOp",EDGE,"E7.5.4"),sQuery(id+"F0.wireOp",EDGE,"E7.6.0"),sQuery(id+"F0.wireOp",EDGE,"E7.6.1"),sQuery(id+"F0.wireOp",EDGE,"E7.6.2"),sQuery(id+"F0.wireOp",EDGE,"E7.6.3"),sQuery(id+"F0.wireOp",EDGE,"E7.6.4"),sQuery(id+"F0.wireOp",EDGE,"E7.7.0"),sQuery(id+"F0.wireOp",EDGE,"E7.7.1"),sQuery(id+"F0.wireOp",EDGE,"E7.7.2"),sQuery(id+"F0.wireOp",EDGE,"E7.7.3"),sQuery(id+"F0.wireOp",EDGE,"E7.7.4"),sQuery(id+"F0.wireOp",EDGE,"E7.8.0"),sQuery(id+"F0.wireOp",EDGE,"E7.8.1"),sQuery(id+"F0.wireOp",EDGE,"E7.8.2"),sQuery(id+"F0.wireOp",EDGE,"E7.8.3"),sQuery(id+"F0.wireOp",EDGE,"E7.8.4"),sQuery(id+"F0.wireOp",EDGE,"E7.9.0"),sQuery(id+"F0.wireOp",EDGE,"E7.9.1"),sQuery(id+"F0.wireOp",EDGE,"E7.9.2"),sQuery(id+"F0.wireOp",EDGE,"E7.9.3"),sQuery(id+"F0.wireOp",EDGE,"E7.9.4"),sQuery(id+"F0.wireOp",EDGE,"E7.10.0"),sQuery(id+"F0.wireOp",EDGE,"E7.10.1"),sQuery(id+"F0.wireOp",EDGE,"E7.10.2"),sQuery(id+"F0.wireOp",EDGE,"E7.10.3"),sQuery(id+"F0.wireOp",EDGE,"E7.10.4"),sQuery(id+"F0.wireOp",EDGE,"E7.11.0"),sQuery(id+"F0.wireOp",EDGE,"E7.11.1"),sQuery(id+"F0.wireOp",EDGE,"E7.11.2"),sQuery(id+"F0.wireOp",EDGE,"E7.11.3"),sQuery(id+"F0.wireOp",EDGE,"E7.11.4"),sQuery(id+"F0.wireOp",EDGE,"E7.12.0"),sQuery(id+"F0.wireOp",EDGE,"E7.12.1"),sQuery(id+"F0.wireOp",EDGE,"E7.12.2"),sQuery(id+"F0.wireOp",EDGE,"E7.12.3"),sQuery(id+"F0.wireOp",EDGE,"E7.12.4"),sQuery(id+"F0.wireOp",EDGE,"E7.13.0"),sQuery(id+"F0.wireOp",EDGE,"E7.13.1"),sQuery(id+"F0.wireOp",EDGE,"E7.13.2"),sQuery(id+"F0.wireOp",EDGE,"E7.13.3"),sQuery(id+"F0.wireOp",EDGE,"E7.13.4"),sQuery(id+"F0.wireOp",EDGE,"E7.14.0"),sQuery(id+"F0.wireOp",EDGE,"E7.14.1"),sQuery(id+"F0.wireOp",EDGE,"E7.14.2"),sQuery(id+"F0.wireOp",EDGE,"E7.14.3"),sQuery(id+"F0.wireOp",EDGE,"E7.14.4"),sQuery(id+"F0.wireOp",EDGE,"E7.15.0"),sQuery(id+"F0.wireOp",EDGE,"E7.15.1"),sQuery(id+"F0.wireOp",EDGE,"E7.15.2"),sQuery(id+"F0.wireOp",EDGE,"E7.15.3"),sQuery(id+"F0.wireOp",EDGE,"E7.15.4"),sQuery(id+"F0.wireOp",EDGE,"E7.16.0"),sQuery(id+"F0.wireOp",EDGE,"E7.16.1"),sQuery(id+"F0.wireOp",EDGE,"E7.16.2"),sQuery(id+"F0.wireOp",EDGE,"E7.16.3"),sQuery(id+"F0.wireOp",EDGE,"E7.16.4"),sQuery(id+"F0.wireOp",EDGE,"E7.17.0"),sQuery(id+"F0.wireOp",EDGE,"E7.17.1"),sQuery(id+"F0.wireOp",EDGE,"E7.17.2"),sQuery(id+"F0.wireOp",EDGE,"E7.17.3"),sQuery(id+"F0.wireOp",EDGE,"E7.17.4"),sQuery(id+"F0.wireOp",EDGE,"E7.18.0"),sQuery(id+"F0.wireOp",EDGE,"E7.18.1"),sQuery(id+"F0.wireOp",EDGE,"E7.18.2"),sQuery(id+"F0.wireOp",EDGE,"E7.18.3"),sQuery(id+"F0.wireOp",EDGE,"E7.18.4"),sQuery(id+"F0.wireOp",EDGE,"E7.19.0"),sQuery(id+"F0.wireOp",EDGE,"E7.19.1"),sQuery(id+"F0.wireOp",EDGE,"E7.19.2"),sQuery(id+"F0.wireOp",EDGE,"E7.19.3"),sQuery(id+"F0.wireOp",EDGE,"E7.19.4"),sQuery(id+"F0.wireOp",EDGE,"E7.20.0"),sQuery(id+"F0.wireOp",EDGE,"E7.20.1"),sQuery(id+"F0.wireOp",EDGE,"E7.20.2"),sQuery(id+"F0.wireOp",EDGE,"E7.20.3"),sQuery(id+"F0.wireOp",EDGE,"E7.20.4"),sQuery(id+"F0.wireOp",EDGE,"E7.21.0"),sQuery(id+"F0.wireOp",EDGE,"E7.21.1"),sQuery(id+"F0.wireOp",EDGE,"E7.21.2"),sQuery(id+"F0.wireOp",EDGE,"E7.21.3"),sQuery(id+"F0.wireOp",EDGE,"E7.21.4"),sQuery(id+"F0.wireOp",EDGE,"E7.22.0"),sQuery(id+"F0.wireOp",EDGE,"E7.22.1"),sQuery(id+"F0.wireOp",EDGE,"E7.22.2"),sQuery(id+"F0.wireOp",EDGE,"E7.22.3"),sQuery(id+"F0.wireOp",EDGE,"E7.22.4"),sQuery(id+"F0.wireOp",EDGE,"E7.23.0"),sQuery(id+"F0.wireOp",EDGE,"E7.23.1"),sQuery(id+"F0.wireOp",EDGE,"E7.23.2"),sQuery(id+"F0.wireOp",EDGE,"E7.23.3"),sQuery(id+"F0.wireOp",EDGE,"E7.23.4"),sQuery(id+"F0.wireOp",EDGE,"E7.24.0"),sQuery(id+"F0.wireOp",EDGE,"E7.24.1"),sQuery(id+"F0.wireOp",EDGE,"E7.24.2"),sQuery(id+"F0.wireOp",EDGE,"E7.24.3"),sQuery(id+"F0.wireOp",EDGE,"E7.24.4"),sQuery(id+"F0.wireOp",EDGE,"E7.25.0"),sQuery(id+"F0.wireOp",EDGE,"E7.25.1"),sQuery(id+"F0.wireOp",EDGE,"E7.25.2"),sQuery(id+"F0.wireOp",EDGE,"E7.25.3"),sQuery(id+"F0.wireOp",EDGE,"E7.25.4"),sQuery(id+"F0.wireOp",EDGE,"E7.26.0"),sQuery(id+"F0.wireOp",EDGE,"E7.26.1"),sQuery(id+"F0.wireOp",EDGE,"E7.26.2"),sQuery(id+"F0.wireOp",EDGE,"E7.26.3"),sQuery(id+"F0.wireOp",EDGE,"E7.26.4"),sQuery(id+"F0.wireOp",EDGE,"E7.27.0"),sQuery(id+"F0.wireOp",EDGE,"E7.27.1"),sQuery(id+"F0.wireOp",EDGE,"E7.27.2"),sQuery(id+"F0.wireOp",EDGE,"E7.27.3"),sQuery(id+"F0.wireOp",EDGE,"E7.27.4"),sQuery(id+"F0.wireOp",EDGE,"E7.28.0"),sQuery(id+"F0.wireOp",EDGE,"E7.28.1"),sQuery(id+"F0.wireOp",EDGE,"E7.28.2"),sQuery(id+"F0.wireOp",EDGE,"E7.28.3"),sQuery(id+"F0.wireOp",EDGE,"E7.28.4"),sQuery(id+"F0.wireOp",EDGE,"E7.29.0"),sQuery(id+"F0.wireOp",EDGE,"E7.29.1"),sQuery(id+"F0.wireOp",EDGE,"E7.29.2"),sQuery(id+"F0.wireOp",EDGE,"E7.29.3"),sQuery(id+"F0.wireOp",EDGE,"E7.29.4"),sQuery(id+"F0.wireOp",EDGE,"E7.30.0"),sQuery(id+"F0.wireOp",EDGE,"E7.30.1"),sQuery(id+"F0.wireOp",EDGE,"E7.30.2"),sQuery(id+"F0.wireOp",EDGE,"E7.30.3"),sQuery(id+"F0.wireOp",EDGE,"E7.30.4"),sQuery(id+"F0.wireOp",EDGE,"E7.31.0"),sQuery(id+"F0.wireOp",EDGE,"E7.31.1"),sQuery(id+"F0.wireOp",EDGE,"E7.31.2"),sQuery(id+"F0.wireOp",EDGE,"E7.31.3"),sQuery(id+"F0.wireOp",EDGE,"E7.31.4"),sQuery(id+"F0.wireOp",EDGE,"E7.32.0"),sQuery(id+"F0.wireOp",EDGE,"E7.32.1"),sQuery(id+"F0.wireOp",EDGE,"E7.32.2"),sQuery(id+"F0.wireOp",EDGE,"E7.32.3"),sQuery(id+"F0.wireOp",EDGE,"E7.32.4"),sQuery(id+"F0.wireOp",EDGE,"E7.33.0"),sQuery(id+"F0.wireOp",EDGE,"E7.33.1"),sQuery(id+"F0.wireOp",EDGE,"E7.33.2"),sQuery(id+"F0.wireOp",EDGE,"E7.33.3"),sQuery(id+"F0.wireOp",EDGE,"E7.33.4"),sQuery(id+"F0.wireOp",EDGE,"E7.34.0"),sQuery(id+"F0.wireOp",EDGE,"E7.34.1"),sQuery(id+"F0.wireOp",EDGE,"E7.34.2"),sQuery(id+"F0.wireOp",EDGE,"E7.34.3"),sQuery(id+"F0.wireOp",EDGE,"E7.34.4"),sQuery(id+"F0.wireOp",EDGE,"E7.35.0"),sQuery(id+"F0.wireOp",EDGE,"E7.35.1"),sQuery(id+"F0.wireOp",EDGE,"E7.35.2"),sQuery(id+"F0.wireOp",EDGE,"E7.35.3"),sQuery(id+"F0.wireOp",EDGE,"E7.35.4")])],"isStart":true});
            var sketch = newSketch(context, id + "F12", { "sketchPlane" : qUnion([Q0])});
            skCircle(sketch, "E16", {"center": v(0, 0) * mm, "radius": 7.5 * mm});
            skSolve(sketch);
        }
        {
            var Q0;
            Q0 = qSketchRegion(id + "F12", true);
            extrude(context, id + "F13", {"entities" : qUnion([Q0]), "operationType" : NewBodyOperationType.ADD, "depth" : 25 * mm});
        }
        {
            var Q0;
            Q0=makeQuery(id+"F13.opExtrude","CAP_EDGE",EDGE,{"disambiguationData":[OSD([sQuery(id+"F12.wireOp",EDGE,"E16")])],"isStart":false});
            chamfer(context, id + "F14", {"entities" : qUnion([Q0]), "width" : 1.5 * mm, "tangentPropagation" : true});
        }
    });
